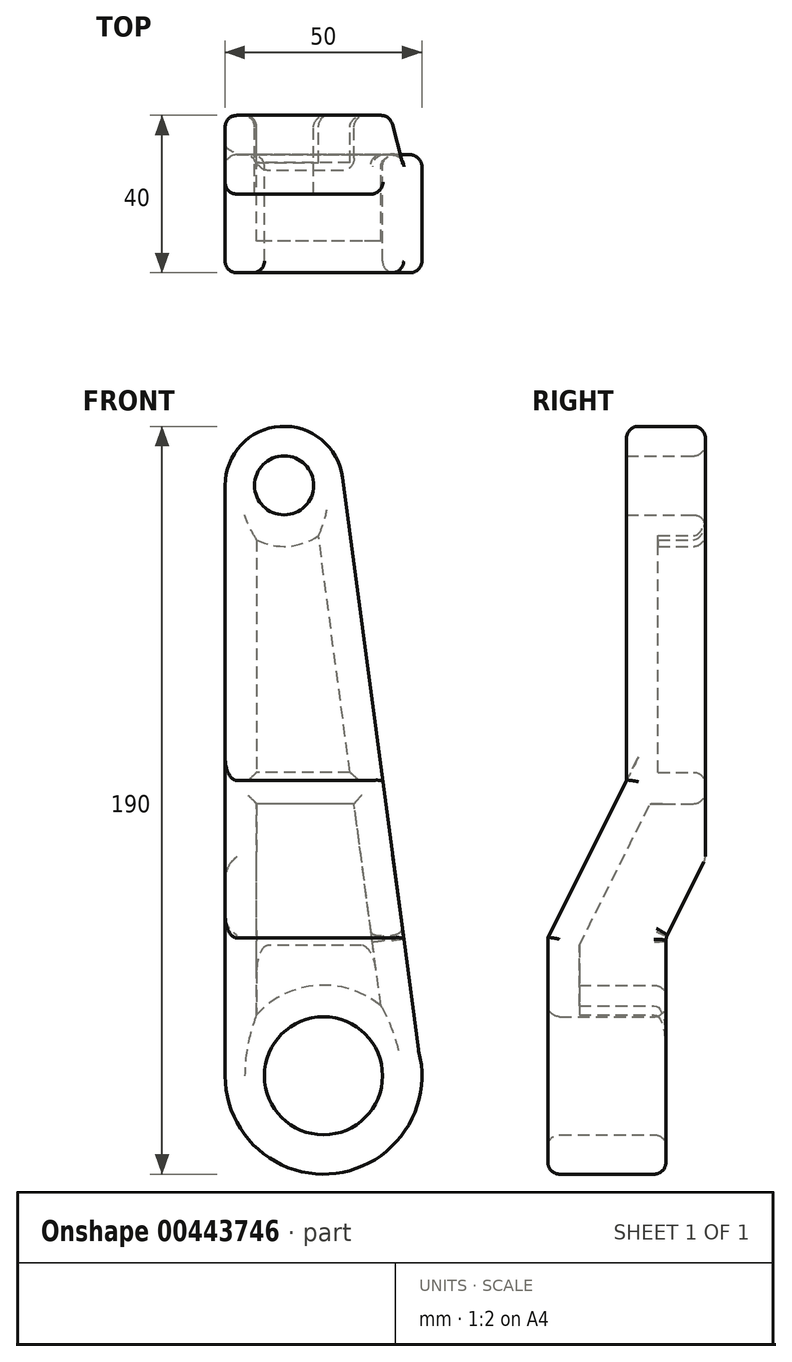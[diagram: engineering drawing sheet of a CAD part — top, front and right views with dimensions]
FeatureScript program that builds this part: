
annotation { "Feature Type Name" : "Feature", "Feature Type Description" : "" }
export const myFeature = defineFeature(function(context is Context, id is Id, definition is map)
    precondition{}
    {
        {
            var Q0;
            Q0=qCreatedBy(makeId("Front.planeOp"),FACE);
            var sketch = newSketch(context, id + "F0", { "sketchPlane" : qUnion([Q0])});
            skCircle(sketch, "E0", {"center": v(0, 0) * mm, "radius": 25 * mm});
            skCircle(sketch, "E1", {"center": v(-10, 150) * mm, "radius": 15 * mm});
            skLineSegment(sketch, "E2", {"start": v(-25, 150) * mm, "end": v(-25, 0) * mm});
            skLineSegment(sketch, "E3", {"start": v(25, 0) * mm, "end": v(4.87, 151.97) * mm});
            skSolve(sketch);
        }
        {
            var Q0;
            Q0 = qSketchRegion(id + "F0", true);
            extrude(context, id + "F1", {"entities" : qUnion([Q0]), "depth" : 40 * mm});
        }
        {
            var Q0;
            Q0=makeQuery(id+"F1.opExtrude","SWEPT_FACE",FACE,{"disambiguationData":[OSD([sQuery(id+"F0.wireOp",EDGE,"E2")])]});
            var sketch = newSketch(context, id + "F2", { "sketchPlane" : qUnion([Q0])});
            skLineSegment(sketch, "E4", {"start": v(0, 55) * mm, "end": v(0, -25.78) * mm});
            skLineSegment(sketch, "E5", {"start": v(10, -25.78) * mm, "end": v(10, 35) * mm});
            skLineSegment(sketch, "E6", {"start": v(10, 35) * mm, "end": v(0, 55) * mm});
            skLineSegment(sketch, "E7", {"start": v(40, 35) * mm, "end": v(20, 75) * mm});
            skLineSegment(sketch, "E8", {"start": v(20, 75) * mm, "end": v(20, 165.97) * mm});
            skLineSegment(sketch, "E9", {"start": v(40, 165.97) * mm, "end": v(40, 150) * mm});
            skLineSegment(sketch, "E10", {"start": v(40, 150) * mm, "end": v(40, 35) * mm});
            skLineSegment(sketch, "E11", {"start": v(0, -25.78) * mm, "end": v(10, -25.78) * mm});
            skLineSegment(sketch, "E12", {"start": v(20, 165.97) * mm, "end": v(40, 165.97) * mm});
            skSolve(sketch);
        }
        {
            var Q0;
            {var subQ4=sQuery(id+"F2.wireOp",EDGE,"E6");Q0=makeQuery(id+"F2.imprint","IMPRINT",FACE,{"disambiguationData":[TD([[makeQuery(id+"F2.imprint","IMPRINT",EDGE,{"derivedFrom":subQ4}),1.0]])]});}
            var Q1;
            {var subQ3=sQuery(id+"F2.wireOp",EDGE,"E11");Q1=makeQuery(id+"F2.imprint","IMPRINT",FACE,{"disambiguationData":[TD([[makeQuery(id+"F2.imprint","IMPRINT",EDGE,{"derivedFrom":subQ3}),1.0]])]});}
            var Q2;
            {var subQ0=sQuery(id+"F2.wireOp",EDGE,"E7");Q2=makeQuery(id+"F2.imprint","IMPRINT",FACE,{"disambiguationData":[TD([[makeQuery(id+"F2.imprint","IMPRINT",EDGE,{"derivedFrom":subQ0}),-1.0]])]});}
            var Q3;
            {var subQ4=sQuery(id+"F2.wireOp",EDGE,"E9");Q3=makeQuery(id+"F2.imprint","IMPRINT",FACE,{"disambiguationData":[TD([[makeQuery(id+"F2.imprint","IMPRINT",EDGE,{"derivedFrom":subQ4}),-1.0]])]});}
            extrude(context, id + "F3", {"entities" : qUnion([Q0, Q1, Q2, Q3]), "operationType" : NewBodyOperationType.REMOVE, "endBound" : BoundingType.THROUGH_ALL, "oppositeDirection" : true, "depth" : 25 * mm});
        }
        {
            var Q0;
            Q0=makeQuery(id+"F1.opExtrude","CAP_FACE",FACE,{"disambiguationData":[OSD([sQuery(id+"F0.wireOp",EDGE,"E0"),sQuery(id+"F0.wireOp",EDGE,"E1"),sQuery(id+"F0.wireOp",EDGE,"E2"),sQuery(id+"F0.wireOp",EDGE,"E3")])],"isStart":true});
            var sketch = newSketch(context, id + "F4", { "sketchPlane" : qUnion([Q0])});
            skCircle(sketch, "E13", {"center": v(10, 150) * mm, "radius": 7.5 * mm});
            skCircle(sketch, "E14", {"center": v(0, 0) * mm, "radius": 15 * mm});
            skSolve(sketch);
        }
        {
            var Q0;
            Q0 = qSketchRegion(id + "F4", true);
            extrude(context, id + "F5", {"entities" : qUnion([Q0]), "operationType" : NewBodyOperationType.REMOVE, "endBound" : BoundingType.THROUGH_ALL, "oppositeDirection" : true, "depth" : 25 * mm});
        }
        {
            var Q0;
            Q0=makeQuery(id+"F1.opExtrude","CAP_FACE",FACE,{"disambiguationData":[OSD([sQuery(id+"F0.wireOp",EDGE,"E0"),sQuery(id+"F0.wireOp",EDGE,"E1"),sQuery(id+"F0.wireOp",EDGE,"E2"),sQuery(id+"F0.wireOp",EDGE,"E3")])],"isStart":true});
            var Q1;
            Q1=makeQuery(id+"F3.boolean.opBoolean","COPY",FACE,{"derivedFrom":makeQuery(id+"F3.opExtrude","SWEPT_FACE",FACE,{"disambiguationData":[OSD([sQuery(id+"F2.wireOp",EDGE,"E6")])]})});
            var Q2;
            Q2=makeQuery(id+"F3.boolean.opBoolean","COPY",FACE,{"derivedFrom":makeQuery(id+"F3.opExtrude","SWEPT_FACE",FACE,{"disambiguationData":[OSD([sQuery(id+"F2.wireOp",EDGE,"E5")])]})});
            shell(context, id + "F6", {"entities" : qUnion([Q0, Q1, Q2]), "thickness" : 8 * mm});
        }
        {
            var Q0;
            Q0=makeQuery(id+"F1.opExtrude","CAP_FACE",FACE,{"disambiguationData":[OSD([sQuery(id+"F0.wireOp",EDGE,"E0"),sQuery(id+"F0.wireOp",EDGE,"E1"),sQuery(id+"F0.wireOp",EDGE,"E2"),sQuery(id+"F0.wireOp",EDGE,"E3")])],"isStart":true});
            var sketch = newSketch(context, id + "F7", { "sketchPlane" : qUnion([Q0])});
            skLineSegment(sketch, "E15", {"start": v(-6.72, 77.11) * mm, "end": v(17, 77.11) * mm});
            skLineSegment(sketch, "E16", {"start": v(-7.78, 69.11) * mm, "end": v(17, 69.11) * mm});
            skLineSegment(sketch, "E17.0", {"start": v(-7.78, 69.11) * mm, "end": v(-6.72, 77.11) * mm});
            skLineSegment(sketch, "E18.0", {"start": v(17, 136.17) * mm, "end": v(17, 55) * mm});
            skPoint(sketch, "E19.orphan", {"position": v(1.24, 137.2) * mm});
            skPoint(sketch, "E20.orphan", {"position": v(-9.64, 55) * mm});
            skSolve(sketch);
        }
        {
            var Q0;
            Q0 = qSketchRegion(id + "F7", true);
            extrude(context, id + "F8", {"entities" : qUnion([Q0]), "operationType" : NewBodyOperationType.ADD, "endBound" : BoundingType.UP_TO_NEXT, "oppositeDirection" : true, "depth" : 25 * mm});
        }
        {
            var Q0;
            Q0=makeQuery(id+"F1.opExtrude","SWEPT_FACE",FACE,{"disambiguationData":[OSD([sQuery(id+"F0.wireOp",EDGE,"E3")])]});
            var Q1;
            Q1=makeQuery(id+"F1.opExtrude","SWEPT_FACE",FACE,{"disambiguationData":[OSD([sQuery(id+"F0.wireOp",EDGE,"E0")])]});
            var Q2;
            Q2=makeQuery(id+"F3.boolean.opBoolean","COPY",FACE,{"derivedFrom":makeQuery(id+"F3.opExtrude","SWEPT_FACE",FACE,{"disambiguationData":[OSD([sQuery(id+"F2.wireOp",EDGE,"E5")])]})});
            var Q3;
            Q3=makeQuery(id+"F8.boolean.opBoolean","MERGE",FACE,{"derivedFrom":[makeQuery(id+"F1.opExtrude","CAP_FACE",FACE,{"disambiguationData":[OSD([sQuery(id+"F0.wireOp",EDGE,"E0"),sQuery(id+"F0.wireOp",EDGE,"E1"),sQuery(id+"F0.wireOp",EDGE,"E2"),sQuery(id+"F0.wireOp",EDGE,"E3")])],"isStart":true}),makeQuery(id+"F8.opExtrude","CAP_FACE",FACE,{"disambiguationData":[OSD([sQuery(id+"F7.wireOp",EDGE,"E15"),sQuery(id+"F7.wireOp",EDGE,"E16"),sQuery(id+"F7.wireOp",EDGE,"E17.0"),sQuery(id+"F7.wireOp",EDGE,"E18.0")])],"isStart":true})]});
            var Q4;
            Q4=makeQuery(id+"F1.opExtrude","SWEPT_FACE",FACE,{"disambiguationData":[OSD([sQuery(id+"F0.wireOp",EDGE,"E1")])]});
            var Q5;
            Q5=makeQuery(id+"F5.boolean.opBoolean","INTERSECT",EDGE,{"derivedFrom":[makeQuery(id+"F1.opExtrude","CAP_FACE",FACE,{"disambiguationData":[OSD([sQuery(id+"F0.wireOp",EDGE,"E0"),sQuery(id+"F0.wireOp",EDGE,"E1"),sQuery(id+"F0.wireOp",EDGE,"E2"),sQuery(id+"F0.wireOp",EDGE,"E3")])],"isStart":false}),makeQuery(id+"F5.opExtrude","SWEPT_FACE",FACE,{"disambiguationData":[OSD([sQuery(id+"F4.wireOp",EDGE,"E14")])]})]});
            var Q6;
            Q6=makeQuery(id+"F1.opExtrude","CAP_EDGE",EDGE,{"disambiguationData":[OSD([sQuery(id+"F0.wireOp",EDGE,"E2")])],"isStart":false});
            var Q7;
            Q7=makeQuery(id+"F3.boolean.opBoolean","COPY",EDGE,{"derivedFrom":makeQuery(id+"F3.opExtrude","CAP_EDGE",EDGE,{"disambiguationData":[OSD([sQuery(id+"F2.wireOp",EDGE,"E6")])],"isStart":true})});
            var Q8;
            Q8=makeQuery(id+"F3.boolean.opBoolean","COPY",EDGE,{"derivedFrom":makeQuery(id+"F3.opExtrude","CAP_EDGE",EDGE,{"disambiguationData":[OSD([sQuery(id+"F2.wireOp",EDGE,"E7")])],"isStart":true})});
            var Q9;
            Q9=makeQuery(id+"F6.opShell","OFFSET_EDGE",EDGE,{"disambiguationData":[OSD([sQuery(id+"F2.wireOp",EDGE,"E7")])]});
            var Q10;
            Q10=makeQuery(id+"F6.opShell","OFFSET_EDGE",EDGE,{"disambiguationData":[OSD([sQuery(id+"F0.wireOp",EDGE,"E3"),sQuery(id+"F2.wireOp",EDGE,"E6")])]});
            var Q11;
            Q11=makeQuery(id+"F3.boolean.opBoolean","INTERSECT",EDGE,{"derivedFrom":[makeQuery(id+"F1.opExtrude","SWEPT_FACE",FACE,{"disambiguationData":[OSD([sQuery(id+"F0.wireOp",EDGE,"E3")])]}),makeQuery(id+"F3.opExtrude","SWEPT_FACE",FACE,{"disambiguationData":[OSD([sQuery(id+"F2.wireOp",EDGE,"E7")])]})]});
            var Q12;
            Q12=makeQuery(id+"F6.opShell","OFFSET_EDGE",EDGE,{"disambiguationData":[OSD([sQuery(id+"F0.wireOp",EDGE,"E3"),sQuery(id+"F2.wireOp",EDGE,"E7")])]});
            var Q13;
            Q13=makeQuery(id+"F6.opShell","OFFSET_EDGE",EDGE,{"disambiguationData":[OSD([sQuery(id+"F2.wireOp",EDGE,"E6")])]});
            fillet(context, id + "F9", {"entities" : qUnion([Q0, Q1, Q2, Q3, Q4, Q5, Q6, Q7, Q8, Q9, Q10, Q11, Q12, Q13]), "radius" : 3 * mm, "tangentPropagation" : true, "allowEdgeOverflow" : false});
        }
    });
